# Revit family: Edge_TB42_C_Side_Hung_Custom
name_source: partatom
category: Windows
revit_build: Autodesk Revit 2014 (Build: 20130308_1515(x64)
units: mm (PartAtom-declared; Revit-internal decimal feet)

## types (1)
- EDGE-TypeC-SideHung-Custom
    Aluminium Thickness = 1 mm  [stored 0.00328084 ft]
    Area Pane Left = 0.36 m²
    Area Pane Middle = 0.49 m²
    Area Pane Right = 0.36 m²
    Bead SG Gap = 13 mm
    Casement Dimension = 42 mm  [stored 0.137795 ft]
    Custom Sash Left Width = 554 mm  [stored 1.81759 ft]
    Custom Sash Right Width = 554 mm  [stored 1.81759 ft]
    Custom Windload = 1000 mm  [stored 3.28084 ft]
    Custom Window Exterior Offset = 84 mm  [stored 0.275591 ft]
    Custom Window Height = 900 mm  [stored 2.95276 ft]
    Custom Window Width = 1800 mm  [stored 5.90551 ft]
    DG Extrusion Start = 11 mm  [stored 0.0360892 ft]
    DG Gasket Finish = Double Glazing Gasket Material
    DG Thickness Calc = 4 mm  [stored 0.0131234 ft]
    Default Sill Height = 800 mm  [stored 2.62467 ft]
    Depth Bead = 28 mm  [stored 0.0918635 ft]
    Depth Mullion = 43 mm  [stored 0.141076 ft]
    Description = Thermal break casement windows (42mm), Type C side hung custom
    Frame Center Offset = 21 mm  [stored 0.0688976 ft]
    Has Stiffener Cap = No
    Height = 900 mm  [stored 2.95276 ft]
    Height Fixed Panel Center = 840 mm  [stored 2.75591 ft]
    Height Sash = 824 mm  [stored 2.70341 ft]
    Height Sash Opening = 854 mm
    Length Mullion = 900 mm  [stored 2.95276 ft]
    Limit Fixed Pane Width Max = 1500 mm  [stored 4.92126 ft]
    Limit Fixed Pane Width Min = 200 mm  [stored 0.656168 ft]
    Limit Sash Height Max = 1500 mm  [stored 4.92126 ft]
    Limit Sash Height Min = 300 mm  [stored 0.984252 ft]
    Limit Sash Width Max = 700 mm  [stored 2.29659 ft]
    Limit Sash Width Min = 300 mm  [stored 0.984252 ft]
    Limit Window Height Max = 1546 mm  [stored 5.07218 ft]
    Limit Window Height Min = 346 mm
    Limit Window Width Max = 2700 mm
    Limit Window Width Min = 1400 mm
    Manufacturer = Crealco
    Max Pane Area = 0.49 m²
    Max System DG One Piece Thickness = 6 mm  [stored 0.019685 ft]
    Max System DG Unit Thickness = 25 mm  [stored 0.082021 ft]
    Model = Edge
    Mullion Depth Windload Based = 0 mm  [stored 0 ft]
    Offset Bead Center Reversed = 21 mm  [stored 0.0688976 ft]
    Offset Fixed Panel Left = 600 mm  [stored 1.9685 ft]
    Offset Mullion Left Side = 570 mm  [stored 1.87008 ft]
    Offset Mullion Right Side = 570 mm  [stored 1.87008 ft]
    Offset Sash Side = 23 mm  [stored 0.0754593 ft]
    Offset Sash Top = 23 mm  [stored 0.0754593 ft]
    Offset Window Exterior = 105 mm  [stored 0.344488 ft]
    SG Gasket Thickness = 6 mm  [stored 0.019685 ft]
    Sash Center Offset = 18 mm
    Sash Height = 855 mm  [stored 2.80512 ft]
    Sash Overlap = 7 mm  [stored 0.0229659 ft]
    Sash Spacing Inner = 8 mm  [stored 0.0262467 ft]
    Side Hung Left = Yes
    Side Hung Right = No
    URL = http://www.crealco.co.za
    Wall Closure = By host
    Width = 1800 mm  [stored 5.90551 ft]
    Width Bead = 15 mm  [stored 0.0492126 ft]
    Width Fixed Panel Center = 600 mm  [stored 1.9685 ft]
    Width Profile = 30 mm  [stored 0.0984252 ft]
    Width Sash Left = 554 mm  [stored 1.81759 ft]
    Width Sash Left Opening = 524 mm  [stored 1.71916 ft]
    Width Sash Right = 554 mm  [stored 1.81759 ft]
    Width Sash Right Opening = 524 mm  [stored 1.71916 ft]
    Windload Design = 1000 mm  [stored 3.28084 ft]

note: [stored X ft] marks values corroborated as IEEE doubles in the binary element streams (Revit-internal decimal feet)

## geometry (parser evidence)
native form markers: Extrusion x1, Sweep x31
no freeform markers — native parametric forms only
